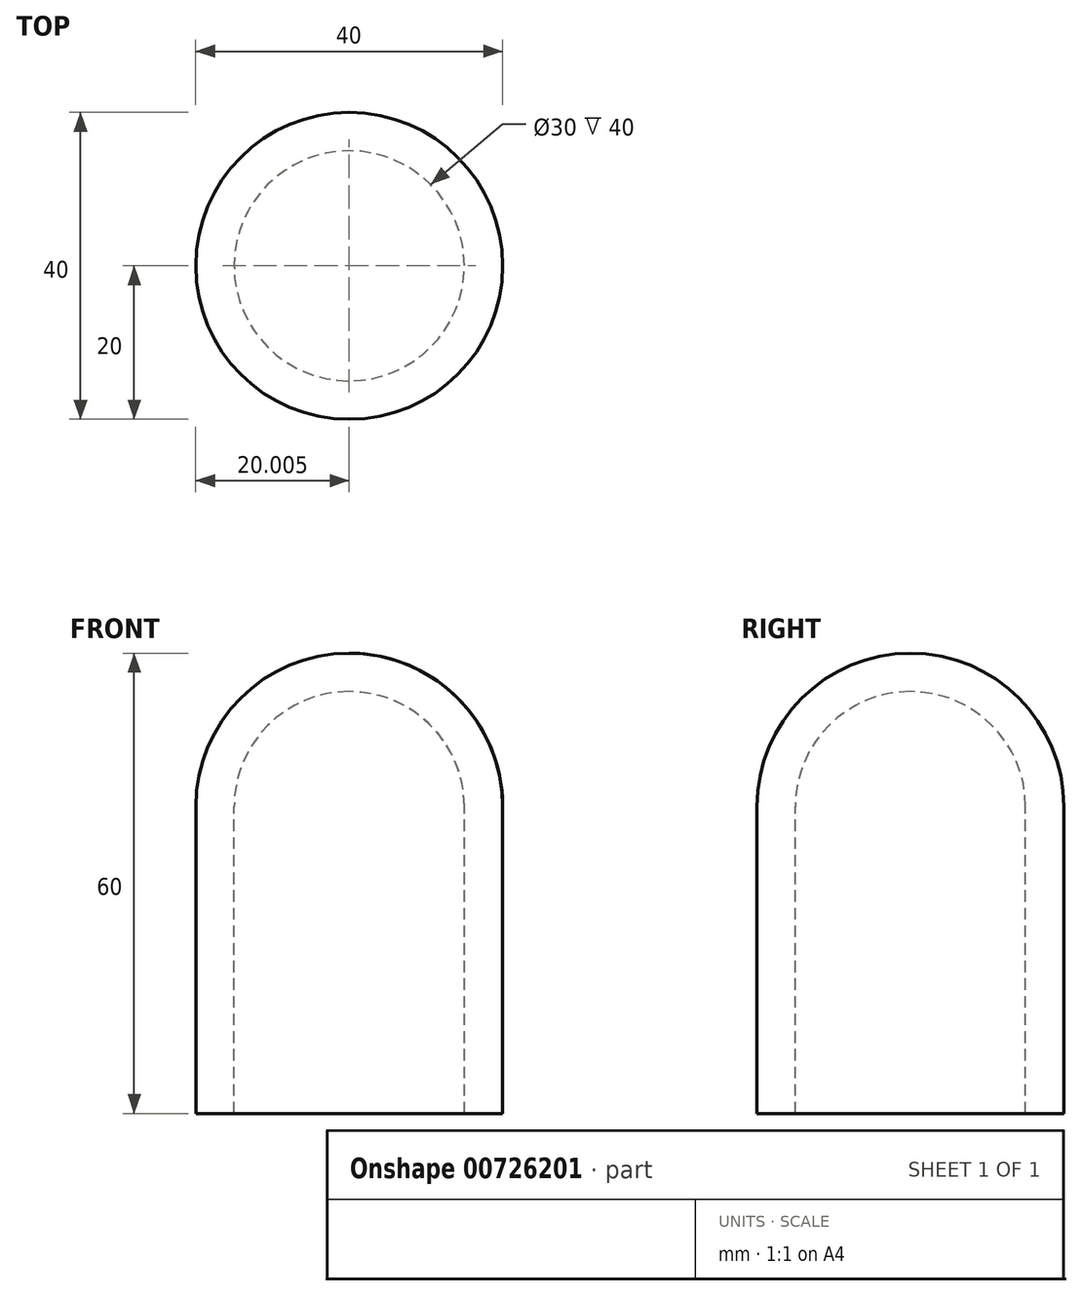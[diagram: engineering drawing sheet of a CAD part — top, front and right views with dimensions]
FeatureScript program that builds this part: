
annotation { "Feature Type Name" : "Feature", "Feature Type Description" : "" }
export const myFeature = defineFeature(function(context is Context, id is Id, definition is map)
    precondition{}
    {
        {
            var Q0;
            Q0=qCreatedBy(makeId("Front.planeOp"),FACE);
            var sketch = newSketch(context, id + "F0", { "sketchPlane" : qUnion([Q0])});
            skArc(sketch, "E0.0", {"start": v(12.64, 9.35) * mm, "mid": v(8.25, 19.96) * mm, "end": v(-2.36, 24.35) * mm});
            skLineSegment(sketch, "E0.1", {"start": v(12.64, -30.65) * mm, "end": v(12.64, 9.35) * mm});
            skArc(sketch, "E1.0", {"start": v(17.64, 9.35) * mm, "mid": v(11.79, 23.5) * mm, "end": v(-2.36, 29.35) * mm});
            skLineSegment(sketch, "E1.1", {"start": v(17.64, -30.65) * mm, "end": v(17.64, 9.35) * mm});
            skLineSegment(sketch, "E2", {"start": v(12.64, -30.65) * mm, "end": v(17.64, -30.65) * mm});
            skLineSegment(sketch, "E3", {"start": v(-2.36, 29.35) * mm, "end": v(-2.36, 24.35) * mm});
            skSolve(sketch);
        }
        {
            var Q0;
            Q0=makeQuery(id+"F0.imprint","IMPRINT",FACE,{"disambiguationData":[TD([[makeQuery(id+"F0.imprint","IMPRINT",EDGE,{"derivedFrom":sQuery(id+"F0.wireOp",EDGE,"E0.0")}),-1.0]])]});
            var Q1;
            Q1=sQuery(id+"F0.wireOp",EDGE,"E3");
            revolve(context, id + "F1", {"surfaceOperationType" : NewSurfaceOperationType.NEW, "entities" : qUnion([Q0]), "axis" : qUnion([Q1]), "revolveType" : RevolveType.FULL});
        }
    });
